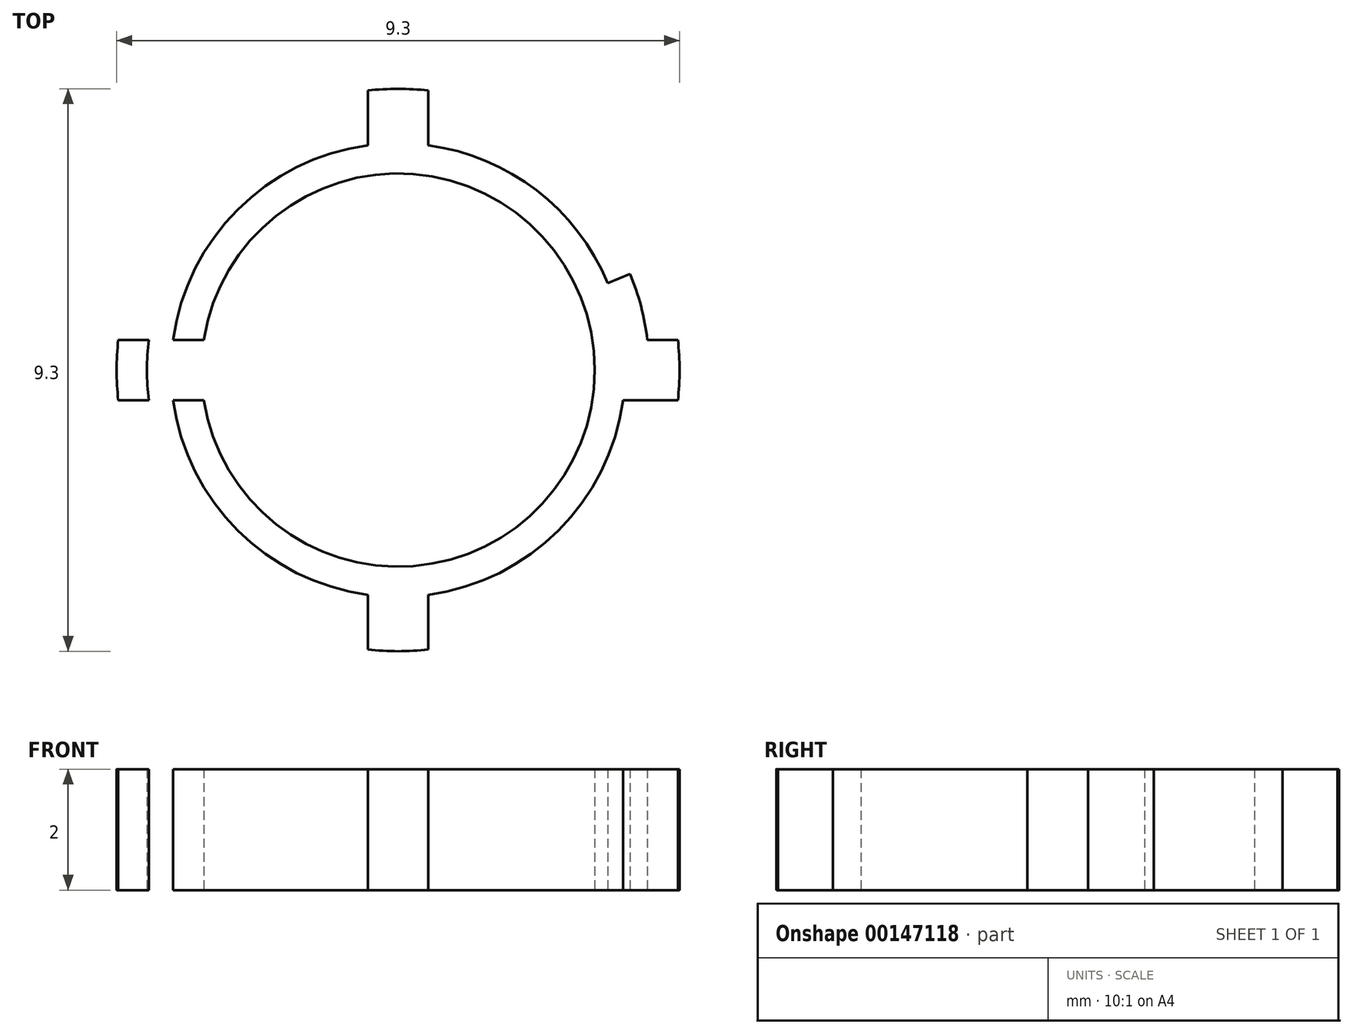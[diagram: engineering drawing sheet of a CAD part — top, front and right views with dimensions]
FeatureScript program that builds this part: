
annotation { "Feature Type Name" : "Feature", "Feature Type Description" : "" }
export const myFeature = defineFeature(function(context is Context, id is Id, definition is map)
    precondition{}
    {
        {
            var Q0;
            Q0=qCreatedBy(makeId("Top.planeOp"),FACE);
            var sketch = newSketch(context, id + "F0", { "sketchPlane" : qUnion([Q0])});
            skCircle(sketch, "E0", {"center": v(0, 0) * mm, "radius": 3.25 * mm});
            skCircle(sketch, "E1", {"center": v(0, 0) * mm, "radius": 3.75 * mm});
            skLineSegment(sketch, "E2", {"start": v(0, 0) * mm, "end": v(0.5, 0) * mm});
            skLineSegment(sketch, "E3", {"start": v(0.5, 0) * mm, "end": v(-0.5, 0) * mm});
            skCircle(sketch, "E4", {"center": v(0, 0) * mm, "radius": 4.65 * mm});
            skCircle(sketch, "E5", {"center": v(0, 0) * mm, "radius": 4.15 * mm});
            skLineSegment(sketch, "E6", {"start": v(-0.5, 0) * mm, "end": v(-0.5, 4.12) * mm});
            skLineSegment(sketch, "E7", {"start": v(0.5, 0) * mm, "end": v(0.5, 4.12) * mm});
            skLineSegment(sketch, "E8", {"start": v(0, 0) * mm, "end": v(0, 4.65) * mm});
            skLineSegment(sketch, "E9", {"start": v(0, 0) * mm, "end": v(1.78, 4.3) * mm});
            skLineSegment(sketch, "E10.MirrorCS", {"start": v(0, 0) * mm, "end": v(-1.78, 4.3) * mm});
            skLineSegment(sketch, "E11.MirrorCS", {"start": v(0, 0) * mm, "end": v(1.78, -4.3) * mm});
            skLineSegment(sketch, "E12.MirrorCS", {"start": v(0, 0) * mm, "end": v(-1.78, -4.3) * mm});
            skLineSegment(sketch, "E13.MirrorCS", {"start": v(0.5, 0) * mm, "end": v(0.5, -4.12) * mm});
            skLineSegment(sketch, "E14.MirrorCS", {"start": v(-0.5, 0) * mm, "end": v(-0.5, -4.12) * mm});
            skLineSegment(sketch, "E15", {"start": v(0, 0) * mm, "end": v(4.3, -1.78) * mm});
            skLineSegment(sketch, "E16", {"start": v(0, 0) * mm, "end": v(-4.3, 1.78) * mm});
            skLineSegment(sketch, "E17", {"start": v(0, 0) * mm, "end": v(0, -0.5) * mm});
            skLineSegment(sketch, "E18", {"start": v(0, -0.5) * mm, "end": v(-4.12, -0.5) * mm});
            skLineSegment(sketch, "E19", {"start": v(0, -0.5) * mm, "end": v(0, 0.5) * mm});
            skLineSegment(sketch, "E20", {"start": v(0, 0.5) * mm, "end": v(-4.12, 0.5) * mm});
            skLineSegment(sketch, "E21", {"start": v(-4.12, 0.5) * mm, "end": v(4.12, 0.5) * mm});
            skLineSegment(sketch, "E22", {"start": v(0, -0.5) * mm, "end": v(4.12, -0.5) * mm});
            skLineSegment(sketch, "E23", {"start": v(0, 0) * mm, "end": v(-4.3, -1.78) * mm});
            skLineSegment(sketch, "E24", {"start": v(0, 0) * mm, "end": v(4.3, 1.78) * mm});
            skLineSegment(sketch, "E25", {"start": v(-4.12, 0.5) * mm, "end": v(-4.62, 0.5) * mm});
            skLineSegment(sketch, "E26", {"start": v(-4.12, -0.5) * mm, "end": v(-4.62, -0.5) * mm});
            skLineSegment(sketch, "E27", {"start": v(-0.5, 4.12) * mm, "end": v(-0.5, 4.62) * mm});
            skLineSegment(sketch, "E28", {"start": v(0.5, 4.12) * mm, "end": v(0.5, 4.62) * mm});
            skLineSegment(sketch, "E29", {"start": v(4.12, 0.5) * mm, "end": v(4.62, 0.5) * mm});
            skLineSegment(sketch, "E30", {"start": v(4.12, -0.5) * mm, "end": v(4.62, -0.5) * mm});
            skLineSegment(sketch, "E31", {"start": v(0.5, -4.12) * mm, "end": v(0.5, -4.62) * mm});
            skLineSegment(sketch, "E32", {"start": v(-0.5, -4.12) * mm, "end": v(-0.5, -4.62) * mm});
            skSolve(sketch);
        }
        {
            var Q0;
            {var subQ2=sQuery(id+"F0.wireOp",EDGE,"E8");var subQ4=sQuery(id+"F0.wireOp",EDGE,"E4");var subQ5=makeQuery(id+"F0.imprint","INTERSECT",VERTEX,{"derivedFrom":[subQ4,subQ2]});Q0=makeQuery(id+"F0.imprint","IMPRINT",FACE,{"disambiguationData":[TD([[makeQuery(id+"F0.imprint","IMPRINT",EDGE,{"disambiguationData":[TD([[subQ5,1.0]])],"derivedFrom":subQ4}),1.0]])]});}
            var Q1;
            {var subQ0=sQuery(id+"F0.wireOp",EDGE,"E8");var subQ1=sQuery(id+"F0.wireOp",EDGE,"E4");var subQ2=makeQuery(id+"F0.imprint","INTERSECT",VERTEX,{"derivedFrom":[subQ1,subQ0]});Q1=makeQuery(id+"F0.imprint","IMPRINT",FACE,{"disambiguationData":[TD([[makeQuery(id+"F0.imprint","IMPRINT",EDGE,{"disambiguationData":[TD([[subQ2,-1.0]])],"derivedFrom":subQ1}),1.0]])]});}
            var Q2;
            {var subQ0=sQuery(id+"F0.wireOp",EDGE,"E8");var subQ1=sQuery(id+"F0.wireOp",EDGE,"E1");var subQ2=makeQuery(id+"F0.imprint","INTERSECT",VERTEX,{"derivedFrom":[subQ1,subQ0]});Q2=makeQuery(id+"F0.imprint","IMPRINT",FACE,{"disambiguationData":[TD([[makeQuery(id+"F0.imprint","IMPRINT",EDGE,{"disambiguationData":[TD([[subQ2,-1.0]])],"derivedFrom":subQ1}),-1.0]])]});}
            var Q3;
            {var subQ0=sQuery(id+"F0.wireOp",EDGE,"E7");var subQ1=sQuery(id+"F0.wireOp",EDGE,"E1");var subQ2=makeQuery(id+"F0.imprint","INTERSECT",VERTEX,{"derivedFrom":[subQ1,subQ0]});Q3=makeQuery(id+"F0.imprint","IMPRINT",FACE,{"disambiguationData":[TD([[makeQuery(id+"F0.imprint","IMPRINT",EDGE,{"disambiguationData":[TD([[subQ2,-1.0]])],"derivedFrom":subQ1}),-1.0]])]});}
            var Q4;
            {var subQ0=sQuery(id+"F0.wireOp",EDGE,"E7");var subQ1=sQuery(id+"F0.wireOp",EDGE,"E0");var subQ2=makeQuery(id+"F0.imprint","INTERSECT",VERTEX,{"derivedFrom":[subQ1,subQ0]});Q4=makeQuery(id+"F0.imprint","IMPRINT",FACE,{"disambiguationData":[TD([[makeQuery(id+"F0.imprint","IMPRINT",EDGE,{"disambiguationData":[TD([[subQ2,-1.0]])],"derivedFrom":subQ1}),-1.0]])]});}
            var Q5;
            {var subQ0=sQuery(id+"F0.wireOp",EDGE,"E8");var subQ1=sQuery(id+"F0.wireOp",EDGE,"E0");var subQ2=makeQuery(id+"F0.imprint","INTERSECT",VERTEX,{"derivedFrom":[subQ1,subQ0]});Q5=makeQuery(id+"F0.imprint","IMPRINT",FACE,{"disambiguationData":[TD([[makeQuery(id+"F0.imprint","IMPRINT",EDGE,{"disambiguationData":[TD([[subQ2,-1.0]])],"derivedFrom":subQ1}),-1.0]])]});}
            var Q6;
            {var subQ0=sQuery(id+"F0.wireOp",EDGE,"E6");var subQ1=sQuery(id+"F0.wireOp",EDGE,"E0");var subQ2=makeQuery(id+"F0.imprint","INTERSECT",VERTEX,{"derivedFrom":[subQ1,subQ0]});Q6=makeQuery(id+"F0.imprint","IMPRINT",FACE,{"disambiguationData":[TD([[makeQuery(id+"F0.imprint","IMPRINT",EDGE,{"disambiguationData":[TD([[subQ2,-1.0]])],"derivedFrom":subQ1}),-1.0]])]});}
            var Q7;
            {var subQ0=sQuery(id+"F0.wireOp",EDGE,"E9");var subQ1=sQuery(id+"F0.wireOp",EDGE,"E0");var subQ2=makeQuery(id+"F0.imprint","INTERSECT",VERTEX,{"derivedFrom":[subQ1,subQ0]});Q7=makeQuery(id+"F0.imprint","IMPRINT",FACE,{"disambiguationData":[TD([[makeQuery(id+"F0.imprint","IMPRINT",EDGE,{"disambiguationData":[TD([[subQ2,-1.0]])],"derivedFrom":subQ1}),-1.0]])]});}
            var Q8;
            {var subQ0=sQuery(id+"F0.wireOp",EDGE,"E24");var subQ1=sQuery(id+"F0.wireOp",EDGE,"E0");var subQ2=makeQuery(id+"F0.imprint","INTERSECT",VERTEX,{"derivedFrom":[subQ1,subQ0]});Q8=makeQuery(id+"F0.imprint","IMPRINT",FACE,{"disambiguationData":[TD([[makeQuery(id+"F0.imprint","IMPRINT",EDGE,{"disambiguationData":[TD([[subQ2,-1.0]])],"derivedFrom":subQ1}),-1.0]])]});}
            var Q9;
            {var subQ0=sQuery(id+"F0.wireOp",EDGE,"E10.MirrorCS");var subQ1=sQuery(id+"F0.wireOp",EDGE,"E0");var subQ2=makeQuery(id+"F0.imprint","INTERSECT",VERTEX,{"derivedFrom":[subQ1,subQ0]});Q9=makeQuery(id+"F0.imprint","IMPRINT",FACE,{"disambiguationData":[TD([[makeQuery(id+"F0.imprint","IMPRINT",EDGE,{"disambiguationData":[TD([[subQ2,-1.0]])],"derivedFrom":subQ1}),-1.0]])]});}
            var Q10;
            {var subQ0=sQuery(id+"F0.wireOp",EDGE,"E16");var subQ1=sQuery(id+"F0.wireOp",EDGE,"E0");var subQ2=makeQuery(id+"F0.imprint","INTERSECT",VERTEX,{"derivedFrom":[subQ1,subQ0]});Q10=makeQuery(id+"F0.imprint","IMPRINT",FACE,{"disambiguationData":[TD([[makeQuery(id+"F0.imprint","IMPRINT",EDGE,{"disambiguationData":[TD([[subQ2,-1.0]])],"derivedFrom":subQ1}),-1.0]])]});}
            var Q11;
            {var subQ0=sQuery(id+"F0.wireOp",EDGE,"E21");var subQ1=sQuery(id+"F0.wireOp",EDGE,"E0");var subQ2=makeQuery(id+"F0.imprint","INTERSECT",VERTEX,{"disambiguationData":[OD(1.0)],"derivedFrom":[subQ1,subQ0]});Q11=makeQuery(id+"F0.imprint","IMPRINT",FACE,{"disambiguationData":[TD([[makeQuery(id+"F0.imprint","IMPRINT",EDGE,{"disambiguationData":[TD([[subQ2,-1.0]])],"derivedFrom":subQ1}),-1.0]])]});}
            var Q12;
            {var subQ0=sQuery(id+"F0.wireOp",EDGE,"E18");var subQ1=sQuery(id+"F0.wireOp",EDGE,"E0");var subQ2=makeQuery(id+"F0.imprint","INTERSECT",VERTEX,{"derivedFrom":[subQ1,subQ0]});Q12=makeQuery(id+"F0.imprint","IMPRINT",FACE,{"disambiguationData":[TD([[makeQuery(id+"F0.imprint","IMPRINT",EDGE,{"disambiguationData":[TD([[subQ2,-1.0]])],"derivedFrom":subQ1}),-1.0]])]});}
            var Q13;
            {var subQ0=sQuery(id+"F0.wireOp",EDGE,"E24");var subQ1=sQuery(id+"F0.wireOp",EDGE,"E0");var subQ2=makeQuery(id+"F0.imprint","INTERSECT",VERTEX,{"derivedFrom":[subQ1,subQ0]});Q13=makeQuery(id+"F0.imprint","IMPRINT",FACE,{"disambiguationData":[TD([[makeQuery(id+"F0.imprint","IMPRINT",EDGE,{"disambiguationData":[TD([[subQ2,1.0]])],"derivedFrom":subQ1}),-1.0]])]});}
            var Q14;
            {var subQ0=sQuery(id+"F0.wireOp",EDGE,"E24");var subQ1=sQuery(id+"F0.wireOp",EDGE,"E0");var subQ2=makeQuery(id+"F0.imprint","INTERSECT",VERTEX,{"derivedFrom":[subQ1,subQ0]});Q14=makeQuery(id+"F0.imprint","IMPRINT",FACE,{"disambiguationData":[TD([[makeQuery(id+"F0.imprint","IMPRINT",EDGE,{"disambiguationData":[TD([[subQ2,-1.0]])],"derivedFrom":subQ1}),-1.0]])]});}
            var Q15;
            {var subQ0=sQuery(id+"F0.wireOp",EDGE,"E9");var subQ1=sQuery(id+"F0.wireOp",EDGE,"E0");var subQ2=makeQuery(id+"F0.imprint","INTERSECT",VERTEX,{"derivedFrom":[subQ1,subQ0]});Q15=makeQuery(id+"F0.imprint","IMPRINT",FACE,{"disambiguationData":[TD([[makeQuery(id+"F0.imprint","IMPRINT",EDGE,{"disambiguationData":[TD([[subQ2,-1.0]])],"derivedFrom":subQ1}),-1.0]])]});}
            var Q16;
            {var subQ0=sQuery(id+"F0.wireOp",EDGE,"E7");var subQ1=sQuery(id+"F0.wireOp",EDGE,"E0");var subQ2=makeQuery(id+"F0.imprint","INTERSECT",VERTEX,{"derivedFrom":[subQ1,subQ0]});Q16=makeQuery(id+"F0.imprint","IMPRINT",FACE,{"disambiguationData":[TD([[makeQuery(id+"F0.imprint","IMPRINT",EDGE,{"disambiguationData":[TD([[subQ2,-1.0]])],"derivedFrom":subQ1}),-1.0]])]});}
            var Q17;
            {var subQ0=sQuery(id+"F0.wireOp",EDGE,"E8");var subQ1=sQuery(id+"F0.wireOp",EDGE,"E0");var subQ2=makeQuery(id+"F0.imprint","INTERSECT",VERTEX,{"derivedFrom":[subQ1,subQ0]});Q17=makeQuery(id+"F0.imprint","IMPRINT",FACE,{"disambiguationData":[TD([[makeQuery(id+"F0.imprint","IMPRINT",EDGE,{"disambiguationData":[TD([[subQ2,-1.0]])],"derivedFrom":subQ1}),-1.0]])]});}
            var Q18;
            {var subQ0=sQuery(id+"F0.wireOp",EDGE,"E6");var subQ1=sQuery(id+"F0.wireOp",EDGE,"E0");var subQ2=makeQuery(id+"F0.imprint","INTERSECT",VERTEX,{"derivedFrom":[subQ1,subQ0]});Q18=makeQuery(id+"F0.imprint","IMPRINT",FACE,{"disambiguationData":[TD([[makeQuery(id+"F0.imprint","IMPRINT",EDGE,{"disambiguationData":[TD([[subQ2,-1.0]])],"derivedFrom":subQ1}),-1.0]])]});}
            var Q19;
            {var subQ0=sQuery(id+"F0.wireOp",EDGE,"E10.MirrorCS");var subQ1=sQuery(id+"F0.wireOp",EDGE,"E0");var subQ2=makeQuery(id+"F0.imprint","INTERSECT",VERTEX,{"derivedFrom":[subQ1,subQ0]});Q19=makeQuery(id+"F0.imprint","IMPRINT",FACE,{"disambiguationData":[TD([[makeQuery(id+"F0.imprint","IMPRINT",EDGE,{"disambiguationData":[TD([[subQ2,-1.0]])],"derivedFrom":subQ1}),-1.0]])]});}
            var Q20;
            {var subQ0=sQuery(id+"F0.wireOp",EDGE,"E16");var subQ1=sQuery(id+"F0.wireOp",EDGE,"E0");var subQ2=makeQuery(id+"F0.imprint","INTERSECT",VERTEX,{"derivedFrom":[subQ1,subQ0]});Q20=makeQuery(id+"F0.imprint","IMPRINT",FACE,{"disambiguationData":[TD([[makeQuery(id+"F0.imprint","IMPRINT",EDGE,{"disambiguationData":[TD([[subQ2,-1.0]])],"derivedFrom":subQ1}),-1.0]])]});}
            var Q21;
            {var subQ0=sQuery(id+"F0.wireOp",EDGE,"E21");var subQ1=sQuery(id+"F0.wireOp",EDGE,"E0");var subQ2=makeQuery(id+"F0.imprint","INTERSECT",VERTEX,{"disambiguationData":[OD(1.0)],"derivedFrom":[subQ1,subQ0]});Q21=makeQuery(id+"F0.imprint","IMPRINT",FACE,{"disambiguationData":[TD([[makeQuery(id+"F0.imprint","IMPRINT",EDGE,{"disambiguationData":[TD([[subQ2,-1.0]])],"derivedFrom":subQ1}),-1.0]])]});}
            var Q22;
            {var subQ0=sQuery(id+"F0.wireOp",EDGE,"E18");var subQ1=sQuery(id+"F0.wireOp",EDGE,"E0");var subQ2=makeQuery(id+"F0.imprint","INTERSECT",VERTEX,{"derivedFrom":[subQ1,subQ0]});Q22=makeQuery(id+"F0.imprint","IMPRINT",FACE,{"disambiguationData":[TD([[makeQuery(id+"F0.imprint","IMPRINT",EDGE,{"disambiguationData":[TD([[subQ2,-1.0]])],"derivedFrom":subQ1}),-1.0]])]});}
            var Q23;
            {var subQ0=sQuery(id+"F0.wireOp",EDGE,"E23");var subQ1=sQuery(id+"F0.wireOp",EDGE,"E0");var subQ2=makeQuery(id+"F0.imprint","INTERSECT",VERTEX,{"derivedFrom":[subQ1,subQ0]});Q23=makeQuery(id+"F0.imprint","IMPRINT",FACE,{"disambiguationData":[TD([[makeQuery(id+"F0.imprint","IMPRINT",EDGE,{"disambiguationData":[TD([[subQ2,-1.0]])],"derivedFrom":subQ1}),-1.0]])]});}
            var Q24;
            {var subQ0=sQuery(id+"F0.wireOp",EDGE,"E12.MirrorCS");var subQ1=sQuery(id+"F0.wireOp",EDGE,"E0");var subQ2=makeQuery(id+"F0.imprint","INTERSECT",VERTEX,{"derivedFrom":[subQ1,subQ0]});Q24=makeQuery(id+"F0.imprint","IMPRINT",FACE,{"disambiguationData":[TD([[makeQuery(id+"F0.imprint","IMPRINT",EDGE,{"disambiguationData":[TD([[subQ2,-1.0]])],"derivedFrom":subQ1}),-1.0]])]});}
            var Q25;
            {var subQ0=sQuery(id+"F0.wireOp",EDGE,"E14.MirrorCS");var subQ1=sQuery(id+"F0.wireOp",EDGE,"E0");var subQ2=makeQuery(id+"F0.imprint","INTERSECT",VERTEX,{"derivedFrom":[subQ1,subQ0]});Q25=makeQuery(id+"F0.imprint","IMPRINT",FACE,{"disambiguationData":[TD([[makeQuery(id+"F0.imprint","IMPRINT",EDGE,{"disambiguationData":[TD([[subQ2,-1.0]])],"derivedFrom":subQ1}),-1.0]])]});}
            var Q26;
            {var subQ0=sQuery(id+"F0.wireOp",EDGE,"E13.MirrorCS");var subQ1=sQuery(id+"F0.wireOp",EDGE,"E0");var subQ2=makeQuery(id+"F0.imprint","INTERSECT",VERTEX,{"derivedFrom":[subQ1,subQ0]});Q26=makeQuery(id+"F0.imprint","IMPRINT",FACE,{"disambiguationData":[TD([[makeQuery(id+"F0.imprint","IMPRINT",EDGE,{"disambiguationData":[TD([[subQ2,-1.0]])],"derivedFrom":subQ1}),-1.0]])]});}
            var Q27;
            {var subQ0=sQuery(id+"F0.wireOp",EDGE,"E11.MirrorCS");var subQ1=sQuery(id+"F0.wireOp",EDGE,"E0");var subQ2=makeQuery(id+"F0.imprint","INTERSECT",VERTEX,{"derivedFrom":[subQ1,subQ0]});Q27=makeQuery(id+"F0.imprint","IMPRINT",FACE,{"disambiguationData":[TD([[makeQuery(id+"F0.imprint","IMPRINT",EDGE,{"disambiguationData":[TD([[subQ2,-1.0]])],"derivedFrom":subQ1}),-1.0]])]});}
            var Q28;
            {var subQ0=sQuery(id+"F0.wireOp",EDGE,"E15");var subQ1=sQuery(id+"F0.wireOp",EDGE,"E0");var subQ2=makeQuery(id+"F0.imprint","INTERSECT",VERTEX,{"derivedFrom":[subQ1,subQ0]});Q28=makeQuery(id+"F0.imprint","IMPRINT",FACE,{"disambiguationData":[TD([[makeQuery(id+"F0.imprint","IMPRINT",EDGE,{"disambiguationData":[TD([[subQ2,-1.0]])],"derivedFrom":subQ1}),-1.0]])]});}
            var Q29;
            {var subQ0=sQuery(id+"F0.wireOp",EDGE,"E21");var subQ1=sQuery(id+"F0.wireOp",EDGE,"E0");var subQ2=makeQuery(id+"F0.imprint","INTERSECT",VERTEX,{"disambiguationData":[OD(0.0)],"derivedFrom":[subQ1,subQ0]});Q29=makeQuery(id+"F0.imprint","IMPRINT",FACE,{"disambiguationData":[TD([[makeQuery(id+"F0.imprint","IMPRINT",EDGE,{"disambiguationData":[TD([[subQ2,1.0]])],"derivedFrom":subQ1}),-1.0]])]});}
            var Q30;
            {var subQ0=sQuery(id+"F0.wireOp",EDGE,"E12.MirrorCS");var subQ1=sQuery(id+"F0.wireOp",EDGE,"E0");var subQ2=makeQuery(id+"F0.imprint","INTERSECT",VERTEX,{"derivedFrom":[subQ1,subQ0]});Q30=makeQuery(id+"F0.imprint","IMPRINT",FACE,{"disambiguationData":[TD([[makeQuery(id+"F0.imprint","IMPRINT",EDGE,{"disambiguationData":[TD([[subQ2,-1.0]])],"derivedFrom":subQ1}),-1.0]])]});}
            var Q31;
            {var subQ0=sQuery(id+"F0.wireOp",EDGE,"E14.MirrorCS");var subQ1=sQuery(id+"F0.wireOp",EDGE,"E0");var subQ2=makeQuery(id+"F0.imprint","INTERSECT",VERTEX,{"derivedFrom":[subQ1,subQ0]});Q31=makeQuery(id+"F0.imprint","IMPRINT",FACE,{"disambiguationData":[TD([[makeQuery(id+"F0.imprint","IMPRINT",EDGE,{"disambiguationData":[TD([[subQ2,-1.0]])],"derivedFrom":subQ1}),-1.0]])]});}
            var Q32;
            {var subQ0=sQuery(id+"F0.wireOp",EDGE,"E13.MirrorCS");var subQ1=sQuery(id+"F0.wireOp",EDGE,"E0");var subQ2=makeQuery(id+"F0.imprint","INTERSECT",VERTEX,{"derivedFrom":[subQ1,subQ0]});Q32=makeQuery(id+"F0.imprint","IMPRINT",FACE,{"disambiguationData":[TD([[makeQuery(id+"F0.imprint","IMPRINT",EDGE,{"disambiguationData":[TD([[subQ2,-1.0]])],"derivedFrom":subQ1}),-1.0]])]});}
            var Q33;
            {var subQ0=sQuery(id+"F0.wireOp",EDGE,"E11.MirrorCS");var subQ1=sQuery(id+"F0.wireOp",EDGE,"E0");var subQ2=makeQuery(id+"F0.imprint","INTERSECT",VERTEX,{"derivedFrom":[subQ1,subQ0]});Q33=makeQuery(id+"F0.imprint","IMPRINT",FACE,{"disambiguationData":[TD([[makeQuery(id+"F0.imprint","IMPRINT",EDGE,{"disambiguationData":[TD([[subQ2,-1.0]])],"derivedFrom":subQ1}),-1.0]])]});}
            var Q34;
            {var subQ0=sQuery(id+"F0.wireOp",EDGE,"E15");var subQ1=sQuery(id+"F0.wireOp",EDGE,"E0");var subQ2=makeQuery(id+"F0.imprint","INTERSECT",VERTEX,{"derivedFrom":[subQ1,subQ0]});Q34=makeQuery(id+"F0.imprint","IMPRINT",FACE,{"disambiguationData":[TD([[makeQuery(id+"F0.imprint","IMPRINT",EDGE,{"disambiguationData":[TD([[subQ2,-1.0]])],"derivedFrom":subQ1}),-1.0]])]});}
            var Q35;
            {var subQ0=sQuery(id+"F0.wireOp",EDGE,"E21");var subQ1=sQuery(id+"F0.wireOp",EDGE,"E0");var subQ2=makeQuery(id+"F0.imprint","INTERSECT",VERTEX,{"disambiguationData":[OD(0.0)],"derivedFrom":[subQ1,subQ0]});Q35=makeQuery(id+"F0.imprint","IMPRINT",FACE,{"disambiguationData":[TD([[makeQuery(id+"F0.imprint","IMPRINT",EDGE,{"disambiguationData":[TD([[subQ2,1.0]])],"derivedFrom":subQ1}),-1.0]])]});}
            var Q36;
            {var subQ0=sQuery(id+"F0.wireOp",EDGE,"E24");var subQ1=sQuery(id+"F0.wireOp",EDGE,"E0");var subQ2=makeQuery(id+"F0.imprint","INTERSECT",VERTEX,{"derivedFrom":[subQ1,subQ0]});Q36=makeQuery(id+"F0.imprint","IMPRINT",FACE,{"disambiguationData":[TD([[makeQuery(id+"F0.imprint","IMPRINT",EDGE,{"disambiguationData":[TD([[subQ2,1.0]])],"derivedFrom":subQ1}),-1.0]])]});}
            var Q37;
            {var subQ0=sQuery(id+"F0.wireOp",EDGE,"E24");var subQ1=sQuery(id+"F0.wireOp",EDGE,"E0");var subQ2=makeQuery(id+"F0.imprint","INTERSECT",VERTEX,{"derivedFrom":[subQ1,subQ0]});Q37=makeQuery(id+"F0.imprint","IMPRINT",FACE,{"disambiguationData":[TD([[makeQuery(id+"F0.imprint","IMPRINT",EDGE,{"disambiguationData":[TD([[subQ2,-1.0]])],"derivedFrom":subQ1}),-1.0]])]});}
            var Q38;
            {var subQ0=sQuery(id+"F0.wireOp",EDGE,"E9");var subQ1=sQuery(id+"F0.wireOp",EDGE,"E0");var subQ2=makeQuery(id+"F0.imprint","INTERSECT",VERTEX,{"derivedFrom":[subQ1,subQ0]});Q38=makeQuery(id+"F0.imprint","IMPRINT",FACE,{"disambiguationData":[TD([[makeQuery(id+"F0.imprint","IMPRINT",EDGE,{"disambiguationData":[TD([[subQ2,-1.0]])],"derivedFrom":subQ1}),-1.0]])]});}
            var Q39;
            {var subQ0=sQuery(id+"F0.wireOp",EDGE,"E7");var subQ1=sQuery(id+"F0.wireOp",EDGE,"E0");var subQ2=makeQuery(id+"F0.imprint","INTERSECT",VERTEX,{"derivedFrom":[subQ1,subQ0]});Q39=makeQuery(id+"F0.imprint","IMPRINT",FACE,{"disambiguationData":[TD([[makeQuery(id+"F0.imprint","IMPRINT",EDGE,{"disambiguationData":[TD([[subQ2,-1.0]])],"derivedFrom":subQ1}),-1.0]])]});}
            var Q40;
            {var subQ0=sQuery(id+"F0.wireOp",EDGE,"E8");var subQ1=sQuery(id+"F0.wireOp",EDGE,"E0");var subQ2=makeQuery(id+"F0.imprint","INTERSECT",VERTEX,{"derivedFrom":[subQ1,subQ0]});Q40=makeQuery(id+"F0.imprint","IMPRINT",FACE,{"disambiguationData":[TD([[makeQuery(id+"F0.imprint","IMPRINT",EDGE,{"disambiguationData":[TD([[subQ2,-1.0]])],"derivedFrom":subQ1}),-1.0]])]});}
            var Q41;
            {var subQ0=sQuery(id+"F0.wireOp",EDGE,"E6");var subQ1=sQuery(id+"F0.wireOp",EDGE,"E0");var subQ2=makeQuery(id+"F0.imprint","INTERSECT",VERTEX,{"derivedFrom":[subQ1,subQ0]});Q41=makeQuery(id+"F0.imprint","IMPRINT",FACE,{"disambiguationData":[TD([[makeQuery(id+"F0.imprint","IMPRINT",EDGE,{"disambiguationData":[TD([[subQ2,-1.0]])],"derivedFrom":subQ1}),-1.0]])]});}
            var Q42;
            {var subQ0=sQuery(id+"F0.wireOp",EDGE,"E10.MirrorCS");var subQ1=sQuery(id+"F0.wireOp",EDGE,"E0");var subQ2=makeQuery(id+"F0.imprint","INTERSECT",VERTEX,{"derivedFrom":[subQ1,subQ0]});Q42=makeQuery(id+"F0.imprint","IMPRINT",FACE,{"disambiguationData":[TD([[makeQuery(id+"F0.imprint","IMPRINT",EDGE,{"disambiguationData":[TD([[subQ2,-1.0]])],"derivedFrom":subQ1}),-1.0]])]});}
            var Q43;
            {var subQ0=sQuery(id+"F0.wireOp",EDGE,"E16");var subQ1=sQuery(id+"F0.wireOp",EDGE,"E0");var subQ2=makeQuery(id+"F0.imprint","INTERSECT",VERTEX,{"derivedFrom":[subQ1,subQ0]});Q43=makeQuery(id+"F0.imprint","IMPRINT",FACE,{"disambiguationData":[TD([[makeQuery(id+"F0.imprint","IMPRINT",EDGE,{"disambiguationData":[TD([[subQ2,-1.0]])],"derivedFrom":subQ1}),-1.0]])]});}
            var Q44;
            {var subQ0=sQuery(id+"F0.wireOp",EDGE,"E21");var subQ1=sQuery(id+"F0.wireOp",EDGE,"E0");var subQ2=makeQuery(id+"F0.imprint","INTERSECT",VERTEX,{"disambiguationData":[OD(1.0)],"derivedFrom":[subQ1,subQ0]});Q44=makeQuery(id+"F0.imprint","IMPRINT",FACE,{"disambiguationData":[TD([[makeQuery(id+"F0.imprint","IMPRINT",EDGE,{"disambiguationData":[TD([[subQ2,-1.0]])],"derivedFrom":subQ1}),-1.0]])]});}
            var Q45;
            {var subQ0=sQuery(id+"F0.wireOp",EDGE,"E18");var subQ1=sQuery(id+"F0.wireOp",EDGE,"E0");var subQ2=makeQuery(id+"F0.imprint","INTERSECT",VERTEX,{"derivedFrom":[subQ1,subQ0]});Q45=makeQuery(id+"F0.imprint","IMPRINT",FACE,{"disambiguationData":[TD([[makeQuery(id+"F0.imprint","IMPRINT",EDGE,{"disambiguationData":[TD([[subQ2,-1.0]])],"derivedFrom":subQ1}),-1.0]])]});}
            var Q46;
            {var subQ0=sQuery(id+"F0.wireOp",EDGE,"E23");var subQ1=sQuery(id+"F0.wireOp",EDGE,"E0");var subQ2=makeQuery(id+"F0.imprint","INTERSECT",VERTEX,{"derivedFrom":[subQ1,subQ0]});Q46=makeQuery(id+"F0.imprint","IMPRINT",FACE,{"disambiguationData":[TD([[makeQuery(id+"F0.imprint","IMPRINT",EDGE,{"disambiguationData":[TD([[subQ2,-1.0]])],"derivedFrom":subQ1}),-1.0]])]});}
            var Q47;
            {var subQ0=sQuery(id+"F0.wireOp",EDGE,"E12.MirrorCS");var subQ1=sQuery(id+"F0.wireOp",EDGE,"E0");var subQ2=makeQuery(id+"F0.imprint","INTERSECT",VERTEX,{"derivedFrom":[subQ1,subQ0]});Q47=makeQuery(id+"F0.imprint","IMPRINT",FACE,{"disambiguationData":[TD([[makeQuery(id+"F0.imprint","IMPRINT",EDGE,{"disambiguationData":[TD([[subQ2,-1.0]])],"derivedFrom":subQ1}),-1.0]])]});}
            var Q48;
            {var subQ0=sQuery(id+"F0.wireOp",EDGE,"E14.MirrorCS");var subQ1=sQuery(id+"F0.wireOp",EDGE,"E0");var subQ2=makeQuery(id+"F0.imprint","INTERSECT",VERTEX,{"derivedFrom":[subQ1,subQ0]});Q48=makeQuery(id+"F0.imprint","IMPRINT",FACE,{"disambiguationData":[TD([[makeQuery(id+"F0.imprint","IMPRINT",EDGE,{"disambiguationData":[TD([[subQ2,-1.0]])],"derivedFrom":subQ1}),-1.0]])]});}
            var Q49;
            {var subQ0=sQuery(id+"F0.wireOp",EDGE,"E13.MirrorCS");var subQ1=sQuery(id+"F0.wireOp",EDGE,"E0");var subQ2=makeQuery(id+"F0.imprint","INTERSECT",VERTEX,{"derivedFrom":[subQ1,subQ0]});Q49=makeQuery(id+"F0.imprint","IMPRINT",FACE,{"disambiguationData":[TD([[makeQuery(id+"F0.imprint","IMPRINT",EDGE,{"disambiguationData":[TD([[subQ2,-1.0]])],"derivedFrom":subQ1}),-1.0]])]});}
            var Q50;
            {var subQ0=sQuery(id+"F0.wireOp",EDGE,"E11.MirrorCS");var subQ1=sQuery(id+"F0.wireOp",EDGE,"E0");var subQ2=makeQuery(id+"F0.imprint","INTERSECT",VERTEX,{"derivedFrom":[subQ1,subQ0]});Q50=makeQuery(id+"F0.imprint","IMPRINT",FACE,{"disambiguationData":[TD([[makeQuery(id+"F0.imprint","IMPRINT",EDGE,{"disambiguationData":[TD([[subQ2,-1.0]])],"derivedFrom":subQ1}),-1.0]])]});}
            var Q51;
            {var subQ0=sQuery(id+"F0.wireOp",EDGE,"E15");var subQ1=sQuery(id+"F0.wireOp",EDGE,"E0");var subQ2=makeQuery(id+"F0.imprint","INTERSECT",VERTEX,{"derivedFrom":[subQ1,subQ0]});Q51=makeQuery(id+"F0.imprint","IMPRINT",FACE,{"disambiguationData":[TD([[makeQuery(id+"F0.imprint","IMPRINT",EDGE,{"disambiguationData":[TD([[subQ2,-1.0]])],"derivedFrom":subQ1}),-1.0]])]});}
            var Q52;
            {var subQ0=sQuery(id+"F0.wireOp",EDGE,"E21");var subQ1=sQuery(id+"F0.wireOp",EDGE,"E0");var subQ2=makeQuery(id+"F0.imprint","INTERSECT",VERTEX,{"disambiguationData":[OD(0.0)],"derivedFrom":[subQ1,subQ0]});Q52=makeQuery(id+"F0.imprint","IMPRINT",FACE,{"disambiguationData":[TD([[makeQuery(id+"F0.imprint","IMPRINT",EDGE,{"disambiguationData":[TD([[subQ2,1.0]])],"derivedFrom":subQ1}),-1.0]])]});}
            var Q53;
            {var subQ0=sQuery(id+"F0.wireOp",EDGE,"E21");var subQ1=sQuery(id+"F0.wireOp",EDGE,"E1");var subQ2=makeQuery(id+"F0.imprint","INTERSECT",VERTEX,{"disambiguationData":[OD(0.0)],"derivedFrom":[subQ1,subQ0]});Q53=makeQuery(id+"F0.imprint","IMPRINT",FACE,{"disambiguationData":[TD([[makeQuery(id+"F0.imprint","IMPRINT",EDGE,{"disambiguationData":[TD([[subQ2,1.0]])],"derivedFrom":subQ1}),-1.0]])]});}
            var Q54;
            {var subQ0=sQuery(id+"F0.wireOp",EDGE,"E21");var subQ1=sQuery(id+"F0.wireOp",EDGE,"E1");var subQ2=makeQuery(id+"F0.imprint","INTERSECT",VERTEX,{"disambiguationData":[OD(1.0)],"derivedFrom":[subQ1,subQ0]});Q54=makeQuery(id+"F0.imprint","IMPRINT",FACE,{"disambiguationData":[TD([[makeQuery(id+"F0.imprint","IMPRINT",EDGE,{"disambiguationData":[TD([[subQ2,-1.0]])],"derivedFrom":subQ1}),-1.0]])]});}
            var Q55;
            {var subQ0=sQuery(id+"F0.wireOp",EDGE,"E14.MirrorCS");var subQ1=sQuery(id+"F0.wireOp",EDGE,"E1");var subQ2=makeQuery(id+"F0.imprint","INTERSECT",VERTEX,{"derivedFrom":[subQ1,subQ0]});Q55=makeQuery(id+"F0.imprint","IMPRINT",FACE,{"disambiguationData":[TD([[makeQuery(id+"F0.imprint","IMPRINT",EDGE,{"disambiguationData":[TD([[subQ2,-1.0]])],"derivedFrom":subQ1}),-1.0]])]});}
            var Q56;
            {var subQ0=sQuery(id+"F0.wireOp",EDGE,"E29");Q56=makeQuery(id+"F0.imprint","IMPRINT",FACE,{"disambiguationData":[TD([[makeQuery(id+"F0.imprint","IMPRINT",EDGE,{"derivedFrom":subQ0}),-1.0]])]});}
            var Q57;
            {var subQ0=sQuery(id+"F0.wireOp",EDGE,"E25");Q57=makeQuery(id+"F0.imprint","IMPRINT",FACE,{"disambiguationData":[TD([[makeQuery(id+"F0.imprint","IMPRINT",EDGE,{"derivedFrom":subQ0}),1.0]])]});}
            var Q58;
            {var subQ0=sQuery(id+"F0.wireOp",EDGE,"E31");Q58=makeQuery(id+"F0.imprint","IMPRINT",FACE,{"disambiguationData":[TD([[makeQuery(id+"F0.imprint","IMPRINT",EDGE,{"derivedFrom":subQ0}),-1.0]])]});}
            extrude(context, id + "F1", {"entities" : qUnion([Q0, Q1, Q2, Q3, Q4, Q5, Q6, Q7, Q8, Q9, Q10, Q11, Q12, Q13, Q14, Q15, Q16, Q17, Q18, Q19, Q20, Q21, Q22, Q23, Q24, Q25, Q26, Q27, Q28, Q29, Q30, Q31, Q32, Q33, Q34, Q35, Q36, Q37, Q38, Q39, Q40, Q41, Q42, Q43, Q44, Q45, Q46, Q47, Q48, Q49, Q50, Q51, Q52, Q53, Q54, Q55, Q56, Q57, Q58]), "depth" : 2 * mm});
        }
    });
